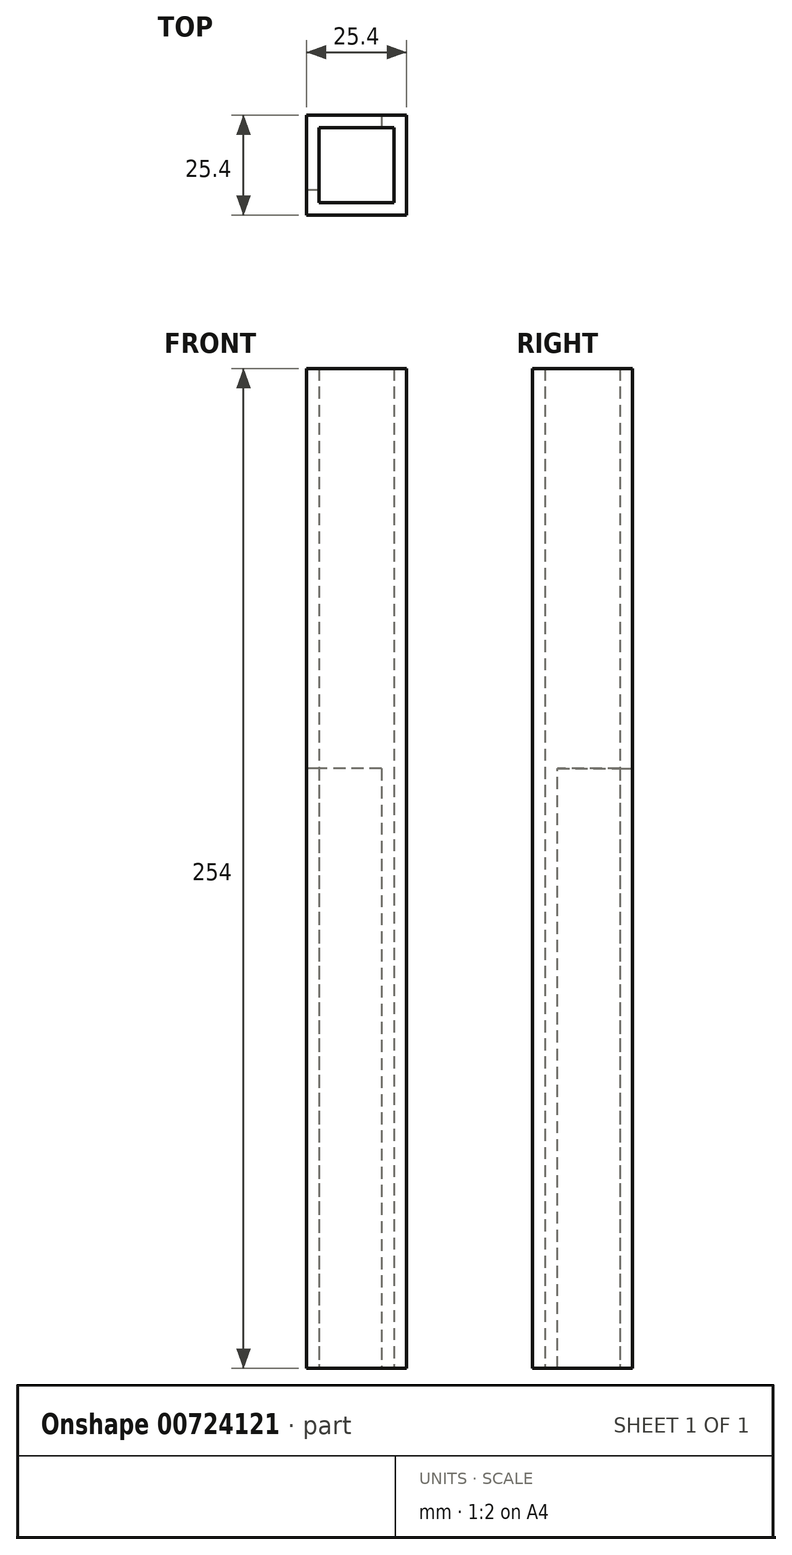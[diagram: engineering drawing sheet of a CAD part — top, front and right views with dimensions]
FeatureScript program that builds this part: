
annotation { "Feature Type Name" : "Feature", "Feature Type Description" : "" }
export const myFeature = defineFeature(function(context is Context, id is Id, definition is map)
    precondition{}
    {
        {
            var Q0;
            Q0=qCreatedBy(makeId("Top.planeOp"),FACE);
            var sketch = newSketch(context, id + "F0", { "sketchPlane" : qUnion([Q0])});
            skLineSegment(sketch, "E0.bottom", {"start": v(12.7, 12.7) * mm, "end": v(-12.7, 12.7) * mm});
            skLineSegment(sketch, "E0.top", {"start": v(12.7, -12.7) * mm, "end": v(-12.7, -12.7) * mm});
            skLineSegment(sketch, "E0.left", {"start": v(12.7, 12.7) * mm, "end": v(12.7, -12.7) * mm});
            skLineSegment(sketch, "E0.right", {"start": v(-12.7, 12.7) * mm, "end": v(-12.7, -12.7) * mm});
            skPoint(sketch, "E0.middle", {"position": v(0, 0) * mm});
            skLineSegment(sketch, "E1.0", {"start": v(9.52, -9.52) * mm, "end": v(-9.53, -9.52) * mm});
            skLineSegment(sketch, "E1.1", {"start": v(9.52, 9.53) * mm, "end": v(9.52, -9.52) * mm});
            skLineSegment(sketch, "E1.2", {"start": v(9.52, 9.53) * mm, "end": v(-9.53, 9.53) * mm});
            skLineSegment(sketch, "E1.3", {"start": v(-9.53, 9.53) * mm, "end": v(-9.53, -9.52) * mm});
            skSolve(sketch);
        }
        {
            var Q0;
            Q0=qSketchRegion(id+"F0",true);
            extrude(context, id + "F1", {"entities" : qUnion([Q0]), "depth" : 254 * mm, "offsetDistance" : 25.4 * mm});
        }
        {
            var Q0;
            Q0=makeQuery(id+"F1.opExtrude","SWEPT_FACE",FACE,{"disambiguationData":[OSD([sQuery(id+"F0.wireOp",EDGE,"E0.right")])]});
            var sketch = newSketch(context, id + "F2", { "sketchPlane" : qUnion([Q0])});
            skLineSegment(sketch, "E2.0", {"start": v(-12.7, 0) * mm, "end": v(6.35, 0) * mm});
            skLineSegment(sketch, "E2.1", {"start": v(-12.7, 152.4) * mm, "end": v(-12.7, 0) * mm});
            skLineSegment(sketch, "E3", {"start": v(6.35, 0) * mm, "end": v(6.35, 152.4) * mm});
            skLineSegment(sketch, "E4", {"start": v(6.35, 152.4) * mm, "end": v(-12.7, 152.4) * mm});
            skPoint(sketch, "E5.orphan", {"position": v(-12.7, 254) * mm});
            skPoint(sketch, "E6.orphan", {"position": v(12.7, 0) * mm});
            skSolve(sketch);
        }
        {
            var Q0;
            Q0=qSketchRegion(id+"F2",true);
            extrude(context, id + "F3", {"entities" : qUnion([Q0]), "operationType" : NewBodyOperationType.REMOVE, "oppositeDirection" : true, "depth" : 19.05 * mm, "offsetDistance" : 25.4 * mm});
        }
    });
